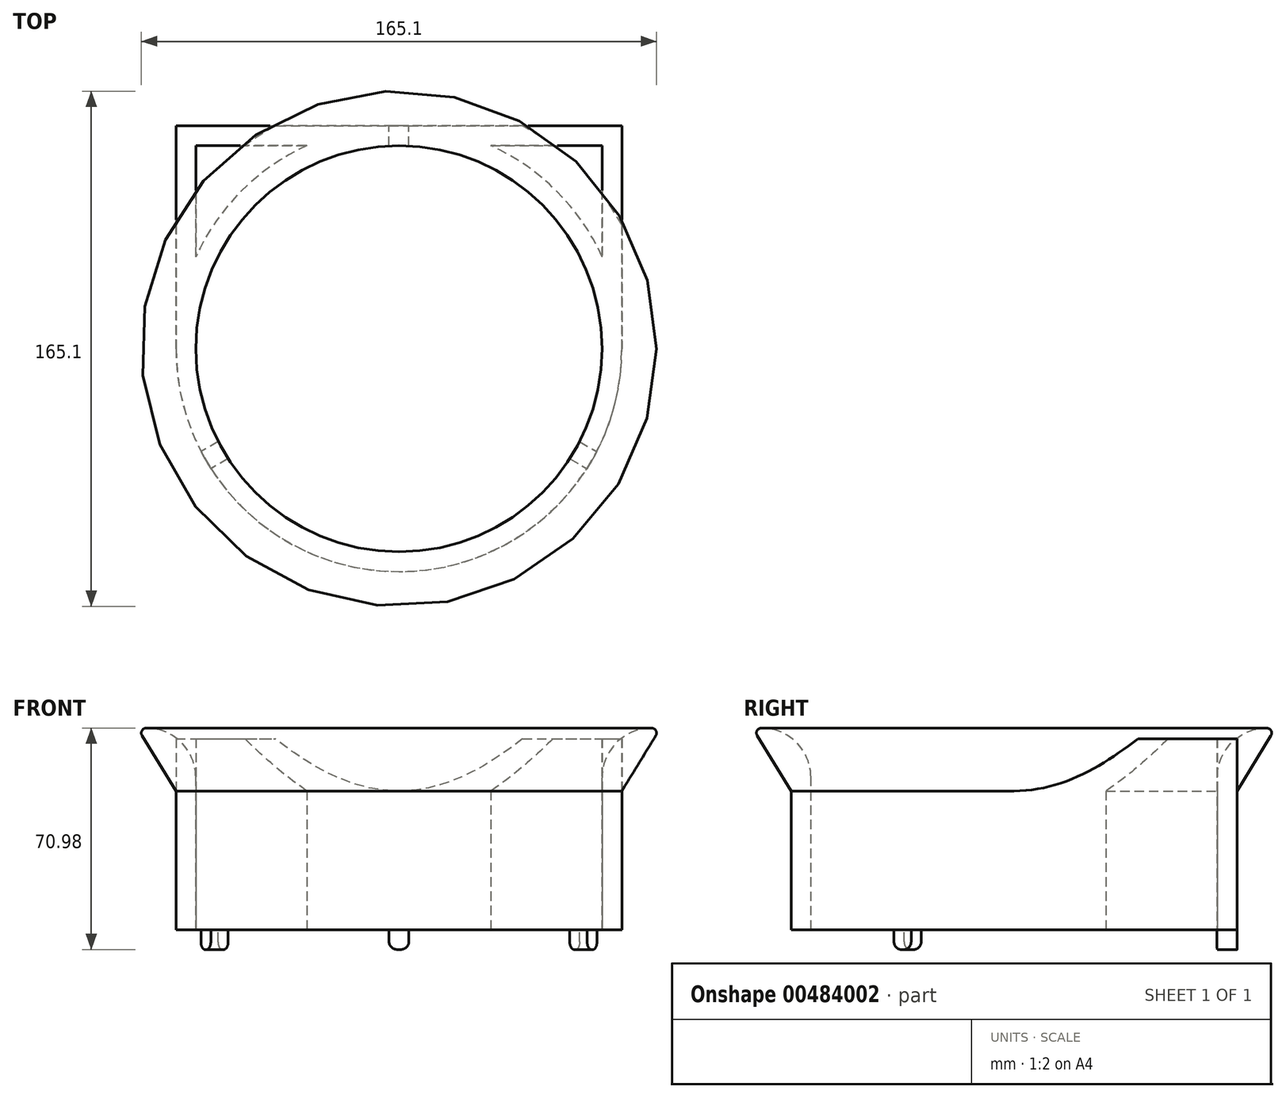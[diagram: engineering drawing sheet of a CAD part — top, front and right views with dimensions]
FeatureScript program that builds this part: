
annotation { "Feature Type Name" : "Feature", "Feature Type Description" : "" }
export const myFeature = defineFeature(function(context is Context, id is Id, definition is map)
    precondition{}
    {
        {
            var Q0;
            Q0=qCreatedBy(makeId("Front.planeOp"),FACE);
            var sketch = newSketch(context, id + "F0", { "sketchPlane" : qUnion([Q0])});
            skArc(sketch, "E0", {"start": v(80.96, 15.88) * mm, "mid": v(69.74, 11.23) * mm, "end": v(65.09, 0) * mm});
            skArc(sketch, "E1.0", {"start": v(80.96, 12.7) * mm, "mid": v(75.74, 11.58) * mm, "end": v(71.44, 8.4) * mm});
            skArc(sketch, "E2", {"start": v(80.96, 12.7) * mm, "mid": v(82.55, 14.29) * mm, "end": v(80.96, 15.88) * mm});
            skLineSegment(sketch, "E3", {"start": v(80.96, 15.88) * mm, "end": v(80.96, 12.7) * mm, "construction": true});
            skLineSegment(sketch, "E4", {"start": v(65.09, 0) * mm, "end": v(71.44, 8.4) * mm});
            skLineSegment(sketch, "E5", {"start": v(0, 47.55) * mm, "end": v(0, -53.2) * mm, "construction": true});
            skLineSegment(sketch, "E6.bottom", {"start": v(71.44, -42.4) * mm, "end": v(65.09, -42.4) * mm});
            skLineSegment(sketch, "E6.top", {"start": v(71.44, -48.75) * mm, "end": v(65.09, -48.75) * mm});
            skLineSegment(sketch, "E6.left", {"start": v(71.44, -42.4) * mm, "end": v(71.44, -48.75) * mm});
            skLineSegment(sketch, "E6.right", {"start": v(65.09, -42.4) * mm, "end": v(65.09, -48.75) * mm});
            skLineSegment(sketch, "E7", {"start": v(65.09, -42.4) * mm, "end": v(65.09, 0) * mm});
            skLineSegment(sketch, "E8", {"start": v(71.44, 8.4) * mm, "end": v(71.44, -42.4) * mm});
            skPoint(sketch, "E9", {"position": v(65.09, -50.8) * mm});
            skLineSegment(sketch, "E10", {"start": v(71.44, -4.3) * mm, "end": v(82.32, 13.46) * mm});
            skSolve(sketch);
        }
        {
            var Q0;
            Q0=makeQuery(id+"F0.imprint","IMPRINT",FACE,{"disambiguationData":[TD([[makeQuery(id+"F0.imprint","IMPRINT",EDGE,{"derivedFrom":sQuery(id+"F0.wireOp",EDGE,"E0")}),1.0]])]});
            var Q1;
            Q1=makeQuery(id+"F0.imprint","IMPRINT",FACE,{"disambiguationData":[TD([[makeQuery(id+"F0.imprint","IMPRINT",EDGE,{"derivedFrom":sQuery(id+"F0.wireOp",EDGE,"E4")}),-1.0]])]});
            var Q2;
            Q2=makeQuery(id+"F0.imprint","IMPRINT",FACE,{"disambiguationData":[TD([[makeQuery(id+"F0.imprint","IMPRINT",EDGE,{"derivedFrom":sQuery(id+"F0.wireOp",EDGE,"E6.bottom")}),1.0]])]});
            var Q3;
            {var subQ0=sQuery(id+"F0.wireOp",EDGE,"E1.0");Q3=makeQuery(id+"F0.imprint","IMPRINT",FACE,{"disambiguationData":[TD([[makeQuery(id+"F0.imprint","IMPRINT",EDGE,{"derivedFrom":subQ0}),1.0]])]});}
            var Q4;
            Q4=sQuery(id+"F0.wireOp",EDGE,"E5");
            revolve(context, id + "F1", {"entities" : qUnion([Q0, Q1, Q2, Q3]), "axis" : qUnion([Q4]), "revolveType" : RevolveType.FULL});
        }
        {
            var Q0;
            Q0=makeQuery(id+"F1.opRevolve","SWEPT_FACE",FACE,{"disambiguationData":[OSD([sQuery(id+"F0.wireOp",EDGE,"E6.top")])]});
            var sketch = newSketch(context, id + "F2", { "sketchPlane" : qUnion([Q0])});
            skLineSegment(sketch, "E11", {"start": v(-178.24, 0) * mm, "end": v(212.04, 0) * mm, "construction": true});
            skLineSegment(sketch, "E12", {"start": v(-71.44, 0) * mm, "end": v(-71.44, -71.44) * mm});
            skLineSegment(sketch, "E13", {"start": v(-71.44, -71.44) * mm, "end": v(71.44, -71.44) * mm});
            skLineSegment(sketch, "E14", {"start": v(71.44, -71.44) * mm, "end": v(71.44, 0) * mm});
            skLineSegment(sketch, "E15", {"start": v(-65.09, -29.44) * mm, "end": v(-65.09, -65.09) * mm});
            skLineSegment(sketch, "E16", {"start": v(-65.09, -65.09) * mm, "end": v(-29.44, -65.09) * mm});
            skLineSegment(sketch, "E17", {"start": v(29.44, -65.09) * mm, "end": v(65.09, -65.09) * mm});
            skLineSegment(sketch, "E18", {"start": v(65.09, -65.09) * mm, "end": v(65.09, -29.44) * mm});
            skArc(sketch, "E19", {"start": v(-71.44, 0) * mm, "mid": v(-69.83, -15.06) * mm, "end": v(-65.09, -29.44) * mm});
            skArc(sketch, "E20", {"start": v(-29.44, -65.09) * mm, "mid": v(-15.06, -69.83) * mm, "end": v(0, -71.44) * mm});
            skArc(sketch, "E21", {"start": v(0, -71.44) * mm, "mid": v(15.06, -69.83) * mm, "end": v(29.44, -65.09) * mm});
            skArc(sketch, "E22", {"start": v(65.09, -29.44) * mm, "mid": v(69.83, -15.06) * mm, "end": v(71.44, 0) * mm});
            skSolve(sketch);
        }
        {
            var Q0;
            {var subQ1=sQuery(id+"F2.wireOp",EDGE,"E12");Q0=makeQuery(id+"F2.imprint","IMPRINT",FACE,{"disambiguationData":[TD([[makeQuery(id+"F2.imprint","IMPRINT",EDGE,{"derivedFrom":subQ1}),1.0]])]});}
            var Q1;
            {var subQ0=sQuery(id+"F2.wireOp",EDGE,"E14");Q1=makeQuery(id+"F2.imprint","IMPRINT",FACE,{"disambiguationData":[TD([[makeQuery(id+"F2.imprint","IMPRINT",EDGE,{"derivedFrom":subQ0}),1.0]])]});}
            extrude(context, id + "F3", {"entities" : qUnion([Q0, Q1]), "operationType" : NewBodyOperationType.ADD, "oppositeDirection" : true, "depth" : 61.2 * mm, "offsetDistance" : 25.4 * mm});
        }
        {
            var Q0;
            {var subQ0=sQuery(id+"F2.wireOp",EDGE,"E13");Q0=makeQuery(id+"F3.boolean.opBoolean","MERGE",FACE,{"derivedFrom":[makeQuery(id+"F1.opRevolve","SWEPT_FACE",FACE,{"disambiguationData":[OSD([sQuery(id+"F0.wireOp",EDGE,"E6.top")])]}),makeQuery(id+"F3.opExtrude","CAP_FACE",FACE,{"disambiguationData":[OSD([sQuery(id+"F2.wireOp",EDGE,"E12"),subQ0,sQuery(id+"F2.wireOp",EDGE,"E15"),sQuery(id+"F2.wireOp",EDGE,"E16"),sQuery(id+"F2.wireOp",EDGE,"E19"),sQuery(id+"F2.wireOp",EDGE,"E20")])],"isStart":true}),makeQuery(id+"F3.opExtrude","CAP_FACE",FACE,{"disambiguationData":[OSD([subQ0,sQuery(id+"F2.wireOp",EDGE,"E14"),sQuery(id+"F2.wireOp",EDGE,"E17"),sQuery(id+"F2.wireOp",EDGE,"E18"),sQuery(id+"F2.wireOp",EDGE,"E21"),sQuery(id+"F2.wireOp",EDGE,"E22")])],"isStart":true})]});}
            var sketch = newSketch(context, id + "F4", { "sketchPlane" : qUnion([Q0])});
            skLineSegment(sketch, "E23", {"start": v(0, -149.39) * mm, "end": v(0, 26.63) * mm, "construction": true});
            skLineSegment(sketch, "E24", {"start": v(-3.18, -65.01) * mm, "end": v(-3.18, -71.44) * mm});
            skLineSegment(sketch, "E25.MirrorCS", {"start": v(3.18, -65.01) * mm, "end": v(3.18, -71.44) * mm});
            skArc(sketch, "E26", {"start": v(-3.18, -65.01) * mm, "mid": v(0, -65.09) * mm, "end": v(3.18, -65.01) * mm});
            skArc(sketch, "E27", {"start": v(-3.18, -71.44) * mm, "mid": v(0, -71.5) * mm, "end": v(3.18, -71.44) * mm});
            skLineSegment(sketch, "E28.1.0", {"start": v(57.89, 29.76) * mm, "end": v(63.45, 32.97) * mm});
            skArc(sketch, "E28.1.1", {"start": v(57.89, 29.76) * mm, "mid": v(56.37, 32.54) * mm, "end": v(54.71, 35.25) * mm});
            skLineSegment(sketch, "E28.1.2", {"start": v(54.71, 35.25) * mm, "end": v(60.28, 38.47) * mm});
            skArc(sketch, "E28.1.3", {"start": v(63.45, 32.97) * mm, "mid": v(61.93, 35.75) * mm, "end": v(60.28, 38.47) * mm});
            skLineSegment(sketch, "E28.2.0", {"start": v(-54.71, 35.25) * mm, "end": v(-60.28, 38.47) * mm});
            skArc(sketch, "E28.2.1", {"start": v(-54.71, 35.25) * mm, "mid": v(-56.37, 32.54) * mm, "end": v(-57.89, 29.76) * mm});
            skLineSegment(sketch, "E28.2.2", {"start": v(-57.89, 29.76) * mm, "end": v(-63.45, 32.97) * mm});
            skArc(sketch, "E28.2.3", {"start": v(-60.28, 38.47) * mm, "mid": v(-61.93, 35.75) * mm, "end": v(-63.45, 32.97) * mm});
            skSolve(sketch);
        }
        {
            var Q0;
            Q0 = qSketchRegion(id + "F4", true);
            extrude(context, id + "F5", {"entities" : qUnion([Q0]), "operationType" : NewBodyOperationType.ADD, "depth" : 6.35 * mm, "offsetDistance" : 25.4 * mm});
        }
        {
            var Q0;
            Q0=makeQuery(id+"F5.opExtrude","CAP_EDGE",EDGE,{"disambiguationData":[OSD([sQuery(id+"F4.wireOp",EDGE,"E28.1.2")])],"isStart":false});
            var Q1;
            Q1=makeQuery(id+"F5.opExtrude","CAP_EDGE",EDGE,{"disambiguationData":[OSD([sQuery(id+"F4.wireOp",EDGE,"E28.1.0")])],"isStart":false});
            var Q2;
            Q2=makeQuery(id+"F5.opExtrude","CAP_EDGE",EDGE,{"disambiguationData":[OSD([sQuery(id+"F4.wireOp",EDGE,"E28.2.0")])],"isStart":false});
            var Q3;
            Q3=makeQuery(id+"F5.opExtrude","CAP_EDGE",EDGE,{"disambiguationData":[OSD([sQuery(id+"F4.wireOp",EDGE,"E28.2.2")])],"isStart":false});
            var Q4;
            Q4=makeQuery(id+"F5.opExtrude","CAP_EDGE",EDGE,{"disambiguationData":[OSD([sQuery(id+"F4.wireOp",EDGE,"E25.MirrorCS")])],"isStart":false});
            var Q5;
            Q5=makeQuery(id+"F5.opExtrude","CAP_EDGE",EDGE,{"disambiguationData":[OSD([sQuery(id+"F4.wireOp",EDGE,"E24")])],"isStart":false});
            fillet(context, id + "F6", {"entities" : qUnion([Q0, Q1, Q2, Q3, Q4, Q5]), "radius" : 2.54 * mm, "tangentPropagation" : true, "allowEdgeOverflow" : false});
        }
    });
